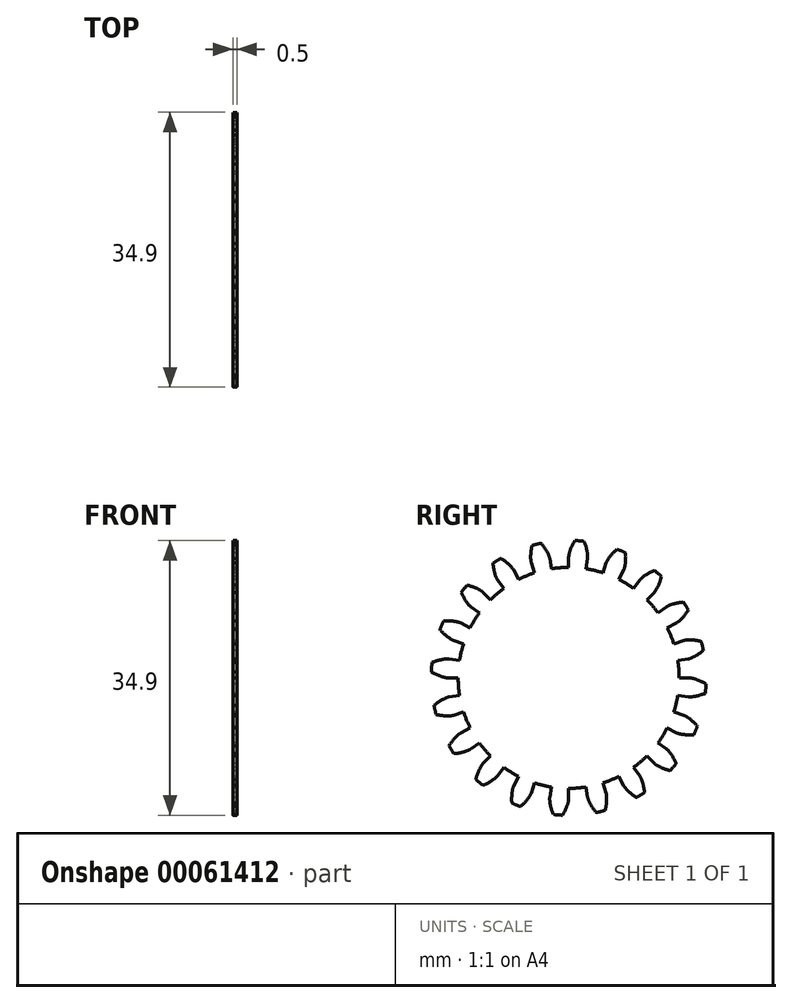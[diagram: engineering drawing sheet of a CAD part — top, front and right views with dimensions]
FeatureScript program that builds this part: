
annotation { "Feature Type Name" : "Feature", "Feature Type Description" : "" }
export const myFeature = defineFeature(function(context is Context, id is Id, definition is map)
    precondition{}
    {
        {
            assignVariable(context, id + "F0", {"name" : "NumberTeeth", "anyValue" : 20});
        }
        {
            assignVariable(context, id + "F1", {"name" : "GearThickness", "anyValue" : .5});
        }
        {
            var Q0;
            Q0=qCreatedBy(makeId("Right.planeOp"),FACE);
            var sketch = newSketch(context, id + "F2", { "sketchPlane" : qUnion([Q0])});
            skCircle(sketch, "E0", {"center": v(0, 0) * mm, "radius": 14.04 * mm});
            skCircle(sketch, "E1", {"center": v(0, 0) * mm, "radius": 15.37 * mm, "construction": true});
            skCircle(sketch, "E2", {"center": v(0, 0) * mm, "radius": 15.88 * mm, "construction": true});
            skCircle(sketch, "E3", {"center": v(0, 0) * mm, "radius": 17.46 * mm});
            skLineSegment(sketch, "E4", {"start": v(0, 0) * mm, "end": v(-15.37, 0) * mm, "construction": true});
            skLineSegment(sketch, "E5.1.0", {"start": v(0, 0) * mm, "end": v(-15.35, 0.77) * mm, "construction": true});
            skLineSegment(sketch, "E5.2.0", {"start": v(0, 0) * mm, "end": v(-15.3, 1.53) * mm, "construction": true});
            skLineSegment(sketch, "E5.3.0", {"start": v(0, 0) * mm, "end": v(-15.2, 2.3) * mm, "construction": true});
            skLineSegment(sketch, "E5.4.0", {"start": v(0, 0) * mm, "end": v(-15.06, 3.05) * mm, "construction": true});
            skLineSegment(sketch, "E5.5.0", {"start": v(0, 0) * mm, "end": v(-14.9, 3.8) * mm, "construction": true});
            skLineSegment(sketch, "E5.6.0", {"start": v(0, 0) * mm, "end": v(-14.68, 4.54) * mm, "construction": true});
            skLineSegment(sketch, "E5.7.0", {"start": v(0, 0) * mm, "end": v(-14.44, 5.27) * mm, "construction": true});
            skLineSegment(sketch, "E5.8.0", {"start": v(0, 0) * mm, "end": v(-14.16, 5.99) * mm, "construction": true});
            skLineSegment(sketch, "E5.9.0", {"start": v(0, 0) * mm, "end": v(-13.84, 6.69) * mm, "construction": true});
            skLineSegment(sketch, "E5.10.0", {"start": v(0, 0) * mm, "end": v(-13.49, 7.37) * mm, "construction": true});
            skLineSegment(sketch, "E5.11.0", {"start": v(0, 0) * mm, "end": v(-13.1, 8.03) * mm, "construction": true});
            skLineSegment(sketch, "E5.12.0", {"start": v(0, 0) * mm, "end": v(-12.68, 8.68) * mm, "construction": true});
            skLineSegment(sketch, "E5.13.0", {"start": v(0, 0) * mm, "end": v(-12.24, 9.3) * mm, "construction": true});
            skLineSegment(sketch, "E5.14.0", {"start": v(0, 0) * mm, "end": v(-11.76, 9.9) * mm, "construction": true});
            skLineSegment(sketch, "E5.anchor2", {"start": v(0, 0) * mm, "end": v(-11.76, 9.9) * mm, "construction": true});
            skLineSegment(sketch, "E6", {"start": v(-15.35, 0.77) * mm, "end": v(-15.39, 0) * mm, "construction": true});
            skLineSegment(sketch, "E7", {"start": v(-15.3, 1.53) * mm, "end": v(-15.45, 0) * mm, "construction": true});
            skLineSegment(sketch, "E8", {"start": v(-15.2, 2.3) * mm, "end": v(-15.54, 0.02) * mm, "construction": true});
            skLineSegment(sketch, "E9", {"start": v(-14.9, 3.8) * mm, "end": v(-15.84, 0.08) * mm, "construction": true});
            skLineSegment(sketch, "E10", {"start": v(-14.68, 4.54) * mm, "end": v(-16.05, 0.14) * mm, "construction": true});
            skLineSegment(sketch, "E11", {"start": v(-14.44, 5.27) * mm, "end": v(-16.28, 0.22) * mm, "construction": true});
            skLineSegment(sketch, "E12", {"start": v(-14.16, 5.99) * mm, "end": v(-16.55, 0.32) * mm, "construction": true});
            skLineSegment(sketch, "E13", {"start": v(-13.84, 6.69) * mm, "end": v(-16.85, 0.46) * mm, "construction": true});
            skLineSegment(sketch, "E14", {"start": v(-13.49, 7.37) * mm, "end": v(-17.17, 0.62) * mm, "construction": true});
            skLineSegment(sketch, "E15", {"start": v(-13.1, 8.03) * mm, "end": v(-17.52, 0.83) * mm, "construction": true});
            skLineSegment(sketch, "E16", {"start": v(-15.06, 3.05) * mm, "end": v(-15.67, 0.04) * mm, "construction": true});
            skLineSegment(sketch, "E17", {"start": v(-12.68, 8.68) * mm, "end": v(-17.9, 1.07) * mm, "construction": true});
            skLineSegment(sketch, "E18", {"start": v(-12.24, 9.3) * mm, "end": v(-18.28, 1.35) * mm, "construction": true});
            skLineSegment(sketch, "E19", {"start": v(-11.76, 9.9) * mm, "end": v(-18.69, 1.67) * mm, "construction": true});
            skLineSegment(sketch, "E20", {"start": v(0, 0) * mm, "end": v(-15.32, 1.2) * mm, "construction": true});
            skLineSegment(sketch, "E21", {"start": v(-14.04, 0) * mm, "end": v(-15.37, 0) * mm});
            skLineSegment(sketch, "E22.MirrorCS", {"start": v(-13.87, 2.2) * mm, "end": v(-15.18, 2.4) * mm});
            skFitSpline(sketch, "E23", {"points": [v(-15.37, 0) * mm, v(-15.39, 0) * mm, v(-15.45, 0) * mm, v(-15.54, 0.02) * mm, v(-15.67, 0.04) * mm, v(-15.84, 0.08) * mm, v(-16.05, 0.14) * mm, v(-16.28, 0.22) * mm, v(-16.55, 0.32) * mm, v(-16.85, 0.46) * mm, v(-17.17, 0.62) * mm, v(-17.52, 0.83) * mm, v(-17.9, 1.07) * mm, v(-18.28, 1.35) * mm, v(-18.69, 1.67) * mm], "startDerivative": vector(-0.82, 0) * mm, "endDerivative": vector(-1.2, 1) * mm});
            skLineSegment(sketch, "E24", {"start": v(-18.69, 1.67) * mm, "end": v(-19.04, 1.97) * mm, "construction": true});
            skFitSpline(sketch, "E25.MirrorCS", {"points": [v(-15.18, 2.4) * mm, v(-15.2, 2.4) * mm, v(-15.26, 2.41) * mm, v(-15.35, 2.41) * mm, v(-15.49, 2.41) * mm, v(-15.66, 2.4) * mm, v(-15.87, 2.37) * mm, v(-16.12, 2.33) * mm, v(-16.4, 2.27) * mm, v(-16.71, 2.18) * mm, v(-17.06, 2.07) * mm, v(-17.43, 1.92) * mm, v(-17.84, 1.74) * mm, v(-18.27, 1.53) * mm, v(-18.72, 1.27) * mm], "startDerivative": vector(-0.8, 0.13) * mm, "endDerivative": vector(-1.34, -0.8) * mm});
            skSolve(sketch);
        }
        {
            var Q0;
            {var subQ0=sQuery(id+"F2.wireOp",EDGE,"E0");var subQ27=makeQuery(id+"F2.imprint","INTERSECT",VERTEX,{"derivedFrom":[subQ0,sQuery(id+"F2.wireOp",EDGE,"10ea1024-8cf5-41f5-a75f-a634b86921f3.10.0")]});Q0=makeQuery(id+"F2.imprint","IMPRINT",FACE,{"disambiguationData":[TD([[makeQuery(id+"F2.imprint","IMPRINT",EDGE,{"disambiguationData":[TD([[subQ27,-1.0]])],"derivedFrom":subQ0}),1.0]])]});}
            var Q1;
            {var subQ0=sQuery(id+"F2.wireOp",EDGE,"10ea1024-8cf5-41f5-a75f-a634b86921f3.1.0");Q1=makeQuery(id+"F2.imprint","IMPRINT",FACE,{"disambiguationData":[TD([[makeQuery(id+"F2.imprint","IMPRINT",EDGE,{"derivedFrom":subQ0}),-1.0]])]});}
            var Q2;
            {var subQ7=sQuery(id+"F2.wireOp",EDGE,"10ea1024-8cf5-41f5-a75f-a634b86921f3.2.0");Q2=makeQuery(id+"F2.imprint","IMPRINT",FACE,{"disambiguationData":[TD([[makeQuery(id+"F2.imprint","IMPRINT",EDGE,{"derivedFrom":subQ7}),-1.0]])]});}
            var Q3;
            {var subQ8=sQuery(id+"F2.wireOp",EDGE,"10ea1024-8cf5-41f5-a75f-a634b86921f3.3.0");Q3=makeQuery(id+"F2.imprint","IMPRINT",FACE,{"disambiguationData":[TD([[makeQuery(id+"F2.imprint","IMPRINT",EDGE,{"derivedFrom":subQ8}),-1.0]])]});}
            var Q4;
            {var subQ2=sQuery(id+"F2.wireOp",EDGE,"10ea1024-8cf5-41f5-a75f-a634b86921f3.4.0");Q4=makeQuery(id+"F2.imprint","IMPRINT",FACE,{"disambiguationData":[TD([[makeQuery(id+"F2.imprint","IMPRINT",EDGE,{"derivedFrom":subQ2}),-1.0]])]});}
            var Q5;
            {var subQ8=sQuery(id+"F2.wireOp",EDGE,"10ea1024-8cf5-41f5-a75f-a634b86921f3.5.0");Q5=makeQuery(id+"F2.imprint","IMPRINT",FACE,{"disambiguationData":[TD([[makeQuery(id+"F2.imprint","IMPRINT",EDGE,{"derivedFrom":subQ8}),-1.0]])]});}
            var Q6;
            {var subQ3=sQuery(id+"F2.wireOp",EDGE,"10ea1024-8cf5-41f5-a75f-a634b86921f3.6.0");Q6=makeQuery(id+"F2.imprint","IMPRINT",FACE,{"disambiguationData":[TD([[makeQuery(id+"F2.imprint","IMPRINT",EDGE,{"derivedFrom":subQ3}),-1.0]])]});}
            var Q7;
            {var subQ0=sQuery(id+"F2.wireOp",EDGE,"10ea1024-8cf5-41f5-a75f-a634b86921f3.7.0");Q7=makeQuery(id+"F2.imprint","IMPRINT",FACE,{"disambiguationData":[TD([[makeQuery(id+"F2.imprint","IMPRINT",EDGE,{"derivedFrom":subQ0}),-1.0]])]});}
            var Q8;
            {var subQ5=sQuery(id+"F2.wireOp",EDGE,"10ea1024-8cf5-41f5-a75f-a634b86921f3.8.0");Q8=makeQuery(id+"F2.imprint","IMPRINT",FACE,{"disambiguationData":[TD([[makeQuery(id+"F2.imprint","IMPRINT",EDGE,{"derivedFrom":subQ5}),-1.0]])]});}
            var Q9;
            {var subQ1=sQuery(id+"F2.wireOp",EDGE,"10ea1024-8cf5-41f5-a75f-a634b86921f3.9.0");Q9=makeQuery(id+"F2.imprint","IMPRINT",FACE,{"disambiguationData":[TD([[makeQuery(id+"F2.imprint","IMPRINT",EDGE,{"derivedFrom":subQ1}),-1.0]])]});}
            var Q10;
            {var subQ5=sQuery(id+"F2.wireOp",EDGE,"10ea1024-8cf5-41f5-a75f-a634b86921f3.10.0");Q10=makeQuery(id+"F2.imprint","IMPRINT",FACE,{"disambiguationData":[TD([[makeQuery(id+"F2.imprint","IMPRINT",EDGE,{"derivedFrom":subQ5}),-1.0]])]});}
            var Q11;
            {var subQ8=sQuery(id+"F2.wireOp",EDGE,"10ea1024-8cf5-41f5-a75f-a634b86921f3.11.0");Q11=makeQuery(id+"F2.imprint","IMPRINT",FACE,{"disambiguationData":[TD([[makeQuery(id+"F2.imprint","IMPRINT",EDGE,{"derivedFrom":subQ8}),-1.0]])]});}
            var Q12;
            {var subQ2=sQuery(id+"F2.wireOp",EDGE,"10ea1024-8cf5-41f5-a75f-a634b86921f3.12.0");Q12=makeQuery(id+"F2.imprint","IMPRINT",FACE,{"disambiguationData":[TD([[makeQuery(id+"F2.imprint","IMPRINT",EDGE,{"derivedFrom":subQ2}),-1.0]])]});}
            var Q13;
            {var subQ3=sQuery(id+"F2.wireOp",EDGE,"10ea1024-8cf5-41f5-a75f-a634b86921f3.13.0");Q13=makeQuery(id+"F2.imprint","IMPRINT",FACE,{"disambiguationData":[TD([[makeQuery(id+"F2.imprint","IMPRINT",EDGE,{"derivedFrom":subQ3}),-1.0]])]});}
            var Q14;
            {var subQ0=sQuery(id+"F2.wireOp",EDGE,"10ea1024-8cf5-41f5-a75f-a634b86921f3.14.0");Q14=makeQuery(id+"F2.imprint","IMPRINT",FACE,{"disambiguationData":[TD([[makeQuery(id+"F2.imprint","IMPRINT",EDGE,{"derivedFrom":subQ0}),-1.0]])]});}
            var Q15;
            {var subQ6=sQuery(id+"F2.wireOp",EDGE,"10ea1024-8cf5-41f5-a75f-a634b86921f3.15.0");Q15=makeQuery(id+"F2.imprint","IMPRINT",FACE,{"disambiguationData":[TD([[makeQuery(id+"F2.imprint","IMPRINT",EDGE,{"derivedFrom":subQ6}),-1.0]])]});}
            var Q16;
            {var subQ5=sQuery(id+"F2.wireOp",EDGE,"10ea1024-8cf5-41f5-a75f-a634b86921f3.16.0");Q16=makeQuery(id+"F2.imprint","IMPRINT",FACE,{"disambiguationData":[TD([[makeQuery(id+"F2.imprint","IMPRINT",EDGE,{"derivedFrom":subQ5}),-1.0]])]});}
            var Q17;
            {var subQ7=sQuery(id+"F2.wireOp",EDGE,"10ea1024-8cf5-41f5-a75f-a634b86921f3.17.0");Q17=makeQuery(id+"F2.imprint","IMPRINT",FACE,{"disambiguationData":[TD([[makeQuery(id+"F2.imprint","IMPRINT",EDGE,{"derivedFrom":subQ7}),-1.0]])]});}
            var Q18;
            {var subQ5=sQuery(id+"F2.wireOp",EDGE,"10ea1024-8cf5-41f5-a75f-a634b86921f3.18.0");Q18=makeQuery(id+"F2.imprint","IMPRINT",FACE,{"disambiguationData":[TD([[makeQuery(id+"F2.imprint","IMPRINT",EDGE,{"derivedFrom":subQ5}),-1.0]])]});}
            var Q19;
            {var subQ8=sQuery(id+"F2.wireOp",EDGE,"10ea1024-8cf5-41f5-a75f-a634b86921f3.19.0");Q19=makeQuery(id+"F2.imprint","IMPRINT",FACE,{"disambiguationData":[TD([[makeQuery(id+"F2.imprint","IMPRINT",EDGE,{"derivedFrom":subQ8}),-1.0]])]});}
            var Q20;
            {var subQ8=sQuery(id+"F2.wireOp",EDGE,"E21");Q20=makeQuery(id+"F2.imprint","IMPRINT",FACE,{"disambiguationData":[TD([[makeQuery(id+"F2.imprint","IMPRINT",EDGE,{"derivedFrom":subQ8}),-1.0]])]});}
            extrude(context, id + "F3", {"entities" : qUnion([Q0, Q1, Q2, Q3, Q4, Q5, Q6, Q7, Q8, Q9, Q10, Q11, Q12, Q13, Q14, Q15, Q16, Q17, Q18, Q19, Q20]), "depth" : (getVariable(context, 'GearThickness')) * mm});
        }
        {
            var Q0;
            Q0=makeQuery(id+"F3.opExtrude","SWEPT_FACE",FACE,{"disambiguationData":[OSD([sQuery(id+"F2.wireOp",EDGE,"E25.MirrorCS")])]});
            var Q1;
            Q1=makeQuery(id+"F3.opExtrude","SWEPT_FACE",FACE,{"disambiguationData":[OSD([sQuery(id+"F2.wireOp",EDGE,"E23")])]});
            var Q2;
            Q2=makeQuery(id+"F3.opExtrude","SWEPT_FACE",FACE,{"disambiguationData":[OSD([sQuery(id+"F2.wireOp",EDGE,"E3")])]});
            var Q3;
            Q3=makeQuery(id+"F3.opExtrude","SWEPT_FACE",FACE,{"disambiguationData":[OSD([sQuery(id+"F2.wireOp",EDGE,"E22.MirrorCS")])]});
            var Q4;
            Q4=makeQuery(id+"F3.opExtrude","SWEPT_FACE",FACE,{"disambiguationData":[OSD([sQuery(id+"F2.wireOp",EDGE,"E21")])]});
            var Q5;
            Q5=makeQuery(id+"F3.opExtrude","SWEPT_FACE",FACE,{"disambiguationData":[OSD([sQuery(id+"F2.wireOp",EDGE,"E0")])]});
            circularPattern(context, id + "F4", {"faces" : qUnion([Q0, Q1, Q2, Q3, Q4]), "axis" : qUnion([Q5]), "angle" : 360 * degree, "instanceCount" : round(getVariable(context, 'NumberTeeth')), "equalSpace" : true, "patternType" : PatternType.FACE});
        }
    });
